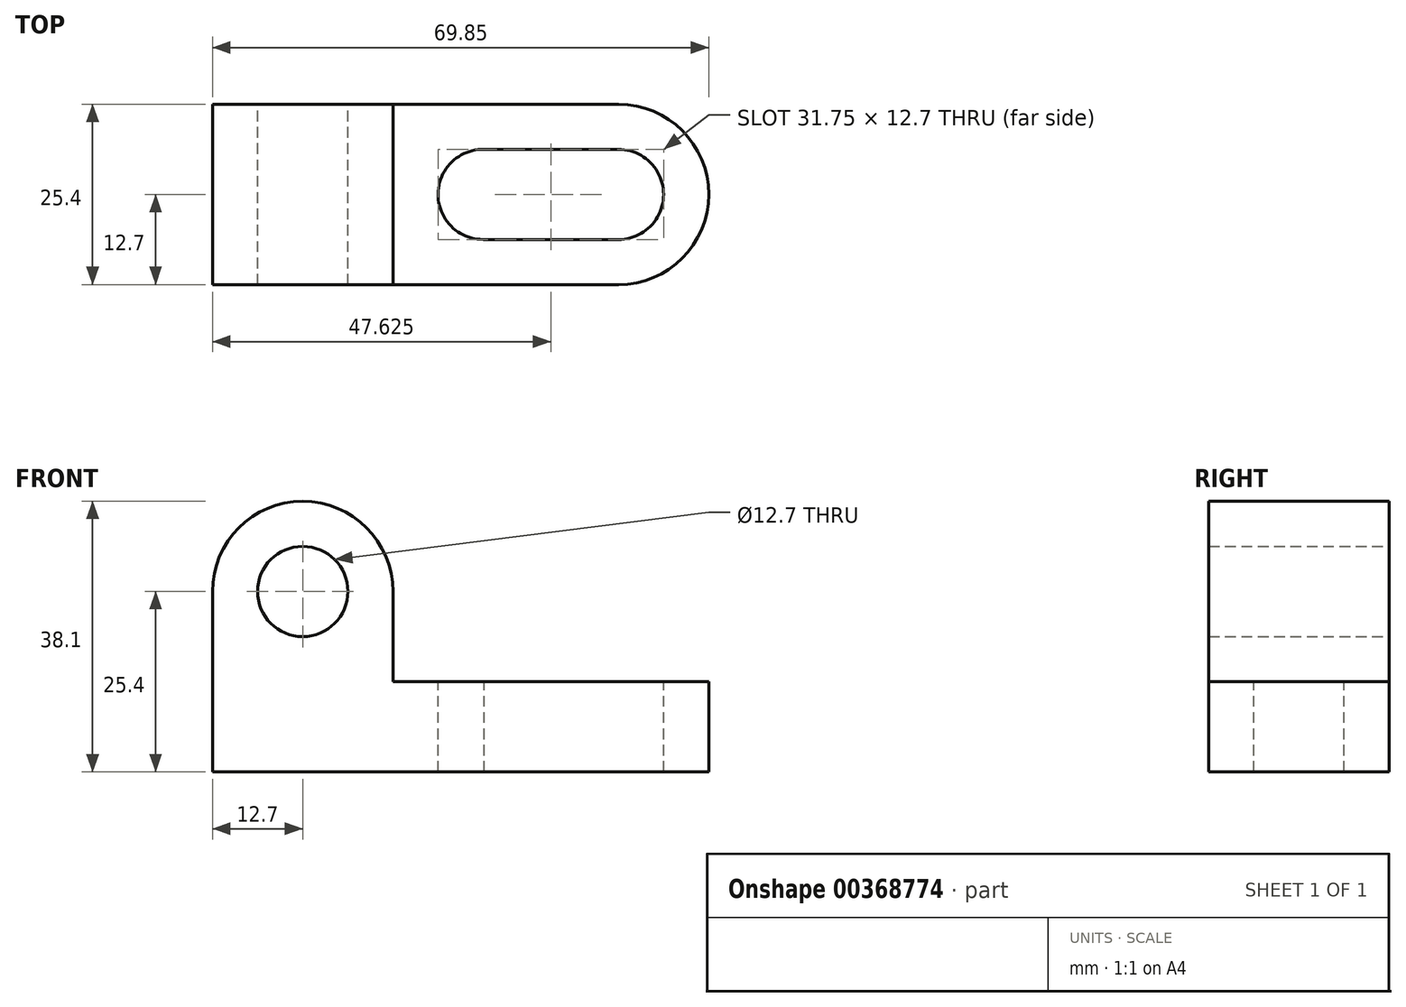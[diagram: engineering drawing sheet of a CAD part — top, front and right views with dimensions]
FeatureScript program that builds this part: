
annotation { "Feature Type Name" : "Feature", "Feature Type Description" : "" }
export const myFeature = defineFeature(function(context is Context, id is Id, definition is map)
    precondition{}
    {
        {
            var Q0;
            Q0=qCreatedBy(makeId("Front.planeOp"),FACE);
            var sketch = newSketch(context, id + "F0", { "sketchPlane" : qUnion([Q0])});
            skLineSegment(sketch, "E0", {"start": v(0, 0) * mm, "end": v(25.4, 0) * mm});
            skLineSegment(sketch, "E1", {"start": v(25.4, 0) * mm, "end": v(25.4, 25.4) * mm});
            skLineSegment(sketch, "E2", {"start": v(0, 25.4) * mm, "end": v(0, 0) * mm});
            skArc(sketch, "E3", {"start": v(25.4, 25.4) * mm, "mid": v(12.7, 38.1) * mm, "end": v(0, 25.4) * mm});
            skCircle(sketch, "E4", {"center": v(12.7, 25.4) * mm, "radius": 6.35 * mm});
            skSolve(sketch);
        }
        {
            var Q0;
            Q0 = qSketchRegion(id + "F0", true);
            extrude(context, id + "F1", {"entities" : qUnion([Q0]), "depth" : 25.4 * mm});
        }
        {
            var Q0;
            Q0=makeQuery(id+"F1.opExtrude","SWEPT_FACE",FACE,{"disambiguationData":[OSD([sQuery(id+"F0.wireOp",EDGE,"E1")])]});
            var sketch = newSketch(context, id + "F2", { "sketchPlane" : qUnion([Q0])});
            skLineSegment(sketch, "E5", {"start": v(-25.4, 0) * mm, "end": v(-25.4, 12.7) * mm});
            skLineSegment(sketch, "E6", {"start": v(-25.4, 12.7) * mm, "end": v(0, 12.7) * mm});
            skLineSegment(sketch, "E7", {"start": v(0, 12.7) * mm, "end": v(0, 0) * mm});
            skLineSegment(sketch, "E8", {"start": v(0, 0) * mm, "end": v(-25.4, 0) * mm});
            skSolve(sketch);
        }
        {
            var Q0;
            Q0 = qSketchRegion(id + "F2", true);
            extrude(context, id + "F3", {"entities" : qUnion([Q0]), "operationType" : NewBodyOperationType.ADD, "depth" : 44.45 * mm});
        }
        {
            var Q0;
            Q0=makeQuery(id+"F3.opExtrude","SWEPT_FACE",FACE,{"disambiguationData":[OSD([sQuery(id+"F2.wireOp",EDGE,"E6")])]});
            var sketch = newSketch(context, id + "F4", { "sketchPlane" : qUnion([Q0])});
            skLineSegment(sketch, "E9", {"start": v(25.4, -12.7) * mm, "end": v(38.1, -12.7) * mm});
            skLineSegment(sketch, "E10", {"start": v(69.85, -12.7) * mm, "end": v(57.15, -12.7) * mm});
            skCircle(sketch, "E11", {"center": v(38.1, -12.7) * mm, "radius": 6.35 * mm});
            skCircle(sketch, "E12", {"center": v(57.15, -12.7) * mm, "radius": 6.35 * mm});
            skLineSegment(sketch, "E13", {"start": v(37.97, -6.35) * mm, "end": v(57.15, -6.35) * mm});
            skLineSegment(sketch, "E14", {"start": v(38.1, -19.05) * mm, "end": v(57.15, -19.05) * mm});
            skSolve(sketch);
        }
        {
            var Q0;
            Q0 = qSketchRegion(id + "F4", true);
            extrude(context, id + "F5", {"entities" : qUnion([Q0]), "operationType" : NewBodyOperationType.REMOVE, "oppositeDirection" : true, "depth" : 25.4 * mm});
        }
        {
            var Q0;
            Q0=makeQuery(id+"F3.opExtrude","CAP_EDGE",EDGE,{"disambiguationData":[OSD([sQuery(id+"F2.wireOp",EDGE,"E5")])],"isStart":false});
            var Q1;
            Q1=makeQuery(id+"F3.opExtrude","CAP_EDGE",EDGE,{"disambiguationData":[OSD([sQuery(id+"F2.wireOp",EDGE,"E7")])],"isStart":false});
            fillet(context, id + "F6", {"entities" : qUnion([Q0, Q1]), "radius" : 12.7 * mm, "tangentPropagation" : true, "allowEdgeOverflow" : false});
        }
    });
